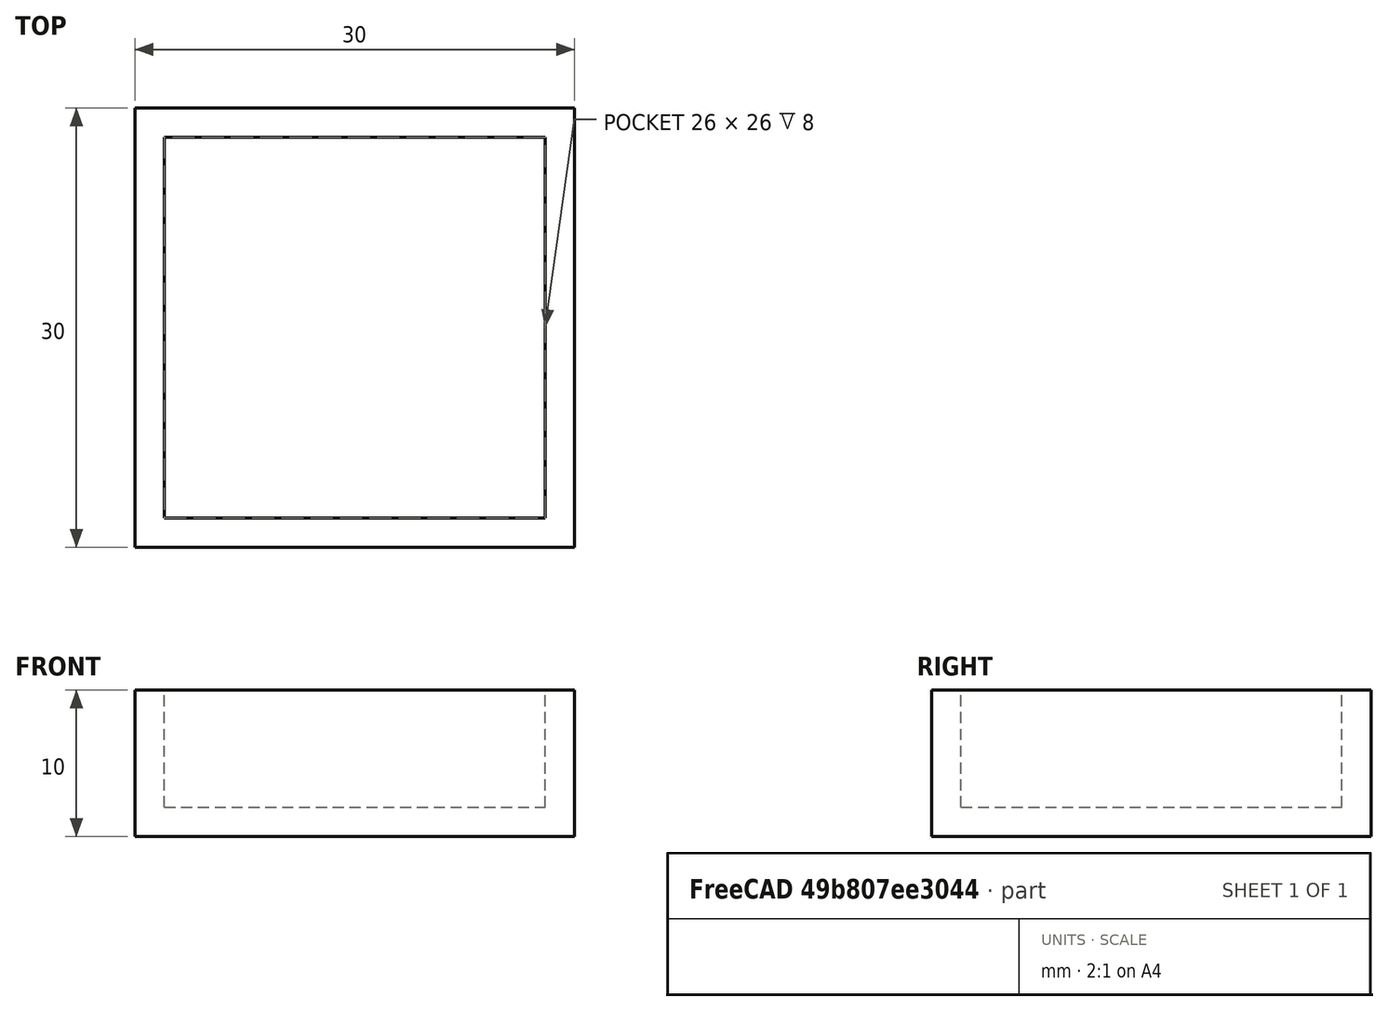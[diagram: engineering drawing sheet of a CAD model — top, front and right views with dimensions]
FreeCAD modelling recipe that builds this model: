
FCSTD DOCUMENT  (FreeCAD 1.0R39109 (Git))
Label: Touch
License: All rights reserved
LicenseURL: http://en.wikipedia.org/wiki/All_rights_reserved
objects: PartDesign::AdditiveBox×1, PartDesign::SubtractiveBox×1, PartDesign::Body×1
note: 7 computed .brp shape members not serialized (recipe doc carries the construction recipe); baked Part::Feature solids carry a one-line shape summary decoded from their .brp

FEATURE [PartDesign::AdditiveBox] Box
  AttacherType = Attacher::AttachEngine3D
  AttachmentSupport = -> [XY_Plane]
  Height = 10
  Length = 30
  MapMode = 5
  Suppressed = false
  Width = 30
FEATURE [PartDesign::SubtractiveBox] Box001
  AttacherType = Attacher::AttachEngine3D
  AttachmentOffset = pos=(2,2,2) rot=(0,0,1;0rad)
  AttachmentSupport = -> [XY_Plane]
  BaseFeature = -> Box
  Height = 8
  Length = 26
  MapMode = 5
  Placement = pos=(2,2,2) rot=(0,0,1;0rad)
  Suppressed = false
  Width = 26
FEATURE [PartDesign::Body] Body
  AllowCompound = false
  Group = -> [Box,Box001]
  Origin = -> Origin
  Tip = -> Box001
